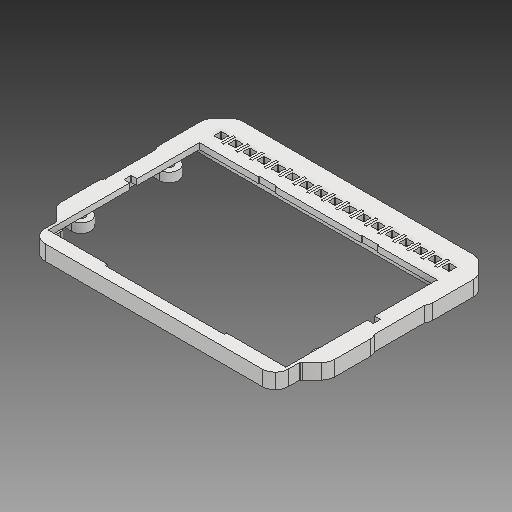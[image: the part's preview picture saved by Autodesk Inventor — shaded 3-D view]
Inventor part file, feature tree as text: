
AUTODESK INVENTOR PART (.ipt)
format: ipt  version: 2017 (Build 210142000, 142)  size: 1,251,840 bytes
history: native  units: mm
features: reference x44, projected_geometry x18, plane x9, sketch x8, extrude x8, other x5, shell x2
ambient origin geometry x8: Origin, YZ Plane, XZ Plane, XY Plane, X Axis, Y Axis, Z Axis, Center Point
bodies: Volumenkörper1 (feature_tree), Volumenkörper2 (feature_tree), Volumenkörper3 (feature_tree)
feature tree (94):
  plane  "Arbeitsebene1"
  sketch  "Skizze1"  dims[d0=10.0mm d1=0.0mm d4=10.0mm d5=0.0mm]
  plane  "Arbeitsebene2"
  extrude  "Extrusion1"  Depth=10.0mm TaperAngle=0.0deg
  plane  "Arbeitsebene3"
  plane  "Arbeitsebene4"
  sketch  "Skizze3"  dims[d8=2.5mm d9=10.0mm d10=0.0mm d11=0.5mm]
  plane  "Arbeitsebene5"
  extrude  "Extrusion2"  Depth=10.0mm TaperAngle=0.0deg
  shell  "Wandung3"  Thickness=0.5mm
  sketch  "Skizze4"  dims[d19=6.0mm d20=6.0mm d23=4.0mm]
  plane  "Arbeitsebene6"
  extrude  "Extrusion3"  Depth=6.0mm
  shell  "Wandung4"  Thickness=4.0mm
  other  "Kombinieren1"
  plane  "Arbeitsebene7"
  sketch  "Skizze7"  dims[d25=4.0mm d26=90.0deg]
  plane  "Arbeitsebene8"
  plane  "Arbeitsebene9"
  extrude  "Extrusion5"  TaperAngle=90.0deg  [1 undecoded]
  extrude  "Extrusion16"  Depth=10.0mm TaperAngle=0.0deg
  extrude  "Extrusion17"  Depth=2.5mm TaperAngle=0.0deg
  extrude  "Extrusion18"  Depth=1.0mm
  extrude  "Extrusion19"  Depth=1.0mm
  reference  "Referenz1"
  reference  "Referenz2"
  reference  "Referenz3"
  reference  "Referenz4"
  reference  "Referenz5"
  reference  "Referenz6"
  reference  "Referenz7"
  reference  "Referenz8"
  reference  "Referenz9"
  reference  "Referenz10"
  reference  "Referenz11"
  reference  "Referenz12"
  reference  "Referenz13"
  reference  "Referenz14"
  reference  "Referenz15"
  reference  "Referenz16"
  reference  "Referenz17"
  reference  "Referenz18"
  projected_geometry  "Projizierte Kontur1"
  reference  "Referenz28"
  reference  "Referenz29"
  reference  "Referenz30"
  projected_geometry  "Projizierte Kontur3"
  reference  "Referenz31"
  reference  "Referenz32"
  sketch  "Skizze23"  dims[d27=180.0deg d28=10.0mm d29=0.0mm]
  sketch  "Skizze24"  dims[d188=2.5mm d189=0.0mm d190=2.5mm d191=0.0mm]
  sketch  "Skizze25"  dims[d196=1.0mm d197=1.0mm]
  projected_geometry  "Projizierte Kontur11"
  reference  "Referenz59"
  projected_geometry  "Projizierte Kontur12"
  projected_geometry  "Projizierte Kontur13"
  projected_geometry  "Projizierte Kontur14"
  projected_geometry  "Projizierte Kontur15"
  projected_geometry  "Projizierte Kontur16"
  projected_geometry  "Projizierte Kontur17"
  projected_geometry  "Projizierte Kontur18"
  projected_geometry  "Projizierte Kontur19"
  projected_geometry  "Projizierte Kontur20"
  projected_geometry  "Projizierte Kontur21"
  projected_geometry  "Projizierte Kontur22"
  projected_geometry  "Projizierte Kontur23"
  projected_geometry  "Projizierte Kontur24"
  projected_geometry  "Projizierte Kontur25"
  projected_geometry  "Projizierte Kontur26"
  sketch  "Skizze26"  dims[d198=1.0mm d199=1.0mm d200=2.5mm d201=0.0mm d202=3.05mm d203=3.05mm d204=0.2mm d205=3.05mm d206=3.05mm d207=0.2mm d208=3.05mm d209=3.05mm d210=0.2mm d211=3.05mm d212=3.05mm d213=0.2mm d214=3.05mm d215=3.05mm d216=0.2mm d217=3.05mm d218=3.05mm d219=0.2mm d220=3.05mm d221=3.05mm d222=0.2mm d223=3.05mm d224=3.05mm d225=0.2mm d226=3.05mm d227=3.05mm d228=0.2mm d229=3.05mm d230=3.05mm d231=0.2mm d232=3.05mm d233=3.05mm d234=0.2mm d235=3.05mm d236=3.05mm d237=0.2mm d238=3.05mm d239=3.05mm d240=0.2mm d241=3.05mm d242=3.05mm d243=0.2mm d244=3.05mm d245=3.05mm d246=0.2mm d247=3.05mm d248=3.05mm d249=0.2mm d250=3.05mm d251=3.05mm d252=0.2mm d253=3.05mm d254=3.05mm d255=0.2mm d256=3.05mm d257=3.05mm d258=0.2mm d259=2.5mm d260=0.0mm]
  reference  "Referenz60"
  reference  "Referenz61"
  reference  "Referenz62"
  reference  "Referenz63"
  reference  "Referenz64"
  reference  "Referenz65"
  reference  "Referenz66"
  reference  "Referenz67"
  reference  "Referenz68"
  reference  "Referenz69"
  reference  "Referenz70"
  reference  "Referenz71"
  reference  "Referenz72"
  reference  "Referenz73"
  reference  "Referenz74"
  reference  "Referenz75"
  reference  "Referenz76"
  reference  "Referenz77"
  reference  "Referenz78"
  reference  "Referenz79"
  other  "<userpath>\Dropbox\Elektronik\aXe_Dashboard240XL\Gehäuse\Gehäuse.iam"
  other  "Gehäuse.iam"
  other  "PCB_SingleLedRow:1"
  other  "Schnittkanten projizieren3"
note: 1 required parameter value undecoded (feature->parameter linkage not recoverable at this tier; creation-order binding heuristic only, values carry confidence <= 0.55)
